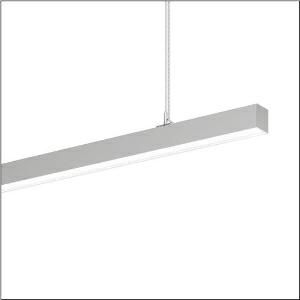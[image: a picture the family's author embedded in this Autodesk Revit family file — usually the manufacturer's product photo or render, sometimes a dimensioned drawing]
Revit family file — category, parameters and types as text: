
# Revit family: silica_r__21_51mx33da37sb_bea4
name_source: partatom
category: Lighting Fixtures
units: mm (PartAtom-declared; Revit-internal decimal feet)

## family parameters
Cut with Voids When Loaded = No
Host = Face
Light Source = No
Part Type = Normal
Room Calculation Point = No
Round Connector Dimension = Use Diameter
Shared = No

## types (1)
- --- (1 x LED, 5910 lm, 41.3 W, 3000K)
    Apparent Load = 41 VA
    CIE Flux Codes = 78 96 99 55 100
    Color Rendering = 80
    Color Temperature = 3000K
    Default Elevation = 1800 mm
    Description = Silica® 21, office luminaire, primary optical cover: prismatic diffuser, of PMMA, CAT 2 (L<= 3000cd/m²), light emission: direct/indirect distribution, primary light characteristic: symmetric, installation type: suspended mounting, LED, rated luminous flux: 5.910lm, luminous efficacy: 143lm/W, light colour: 830, colour temperature: 3000K, with terminal, 3+2-pole, max. 2.5mm², mains connection: 220..240V, AC, 50/60Hz, rated input power: 41.3W, luminaire housing, of aluminium, metallic grey (RAL 9006), length: 1.204mm, width: 53mm, height: 53mm, protection rating (complete): IP20, insulation class (complete): insulation class I (protective earthing), certification: CE, permissible operating ambient temperature: 0..+35°C, standard: EN 50419, packaging unit: 1 piece
    Height = 53 mm
    Lamp = 1 x LED
    Lamp Light Flux = 5910 lm
    Lamp Power = 41.3 W
    Lamp count = 1
    Length = 1204 mm
    Luminous efficacy = 143 lm/W
    Manufacturer = Siteco
    ModVariant = No
    Model = 51MX33DA37SB
    Mounting Place = Ceiling
    Mounting Type = Pendant
    Number of Poles = 1
    OnlyDefault = Yes
    Power Factor = 1
    Product Name = Silica® 21
    Product group = office luminaire | ceiling pendant
    ProductGroupID = 902
    Protection Class = Protection class I
    Protection Degree = IP 20
    RLX_Detail_Level = 1
    RLX_Emergency_Light_Flux = 0 lm
    RLX_Emergency_Type = 0
    RLX_Emergency_Type_DB = No
    RlxData = <blob elided: 23421 chars, md5=ea39089c>
    Socket = socket
    Standby Power = 0 W
    System Light Flux = 5910 lm
    System Power = 41 W
    Type Comments = factory setting: luminous flux: 100 % | dim-lin: 254 | 345 mA
    Type Image = l_1313621.jpg
    URL = http://relux.com
    VarID = @adj_067063
    Voltage = 0 V
    Weight = 0.00 kg
    Width = 53 mm

## geometry (parser evidence)
native form markers: Blend x4, Sweep x12
no freeform markers — native parametric forms only
